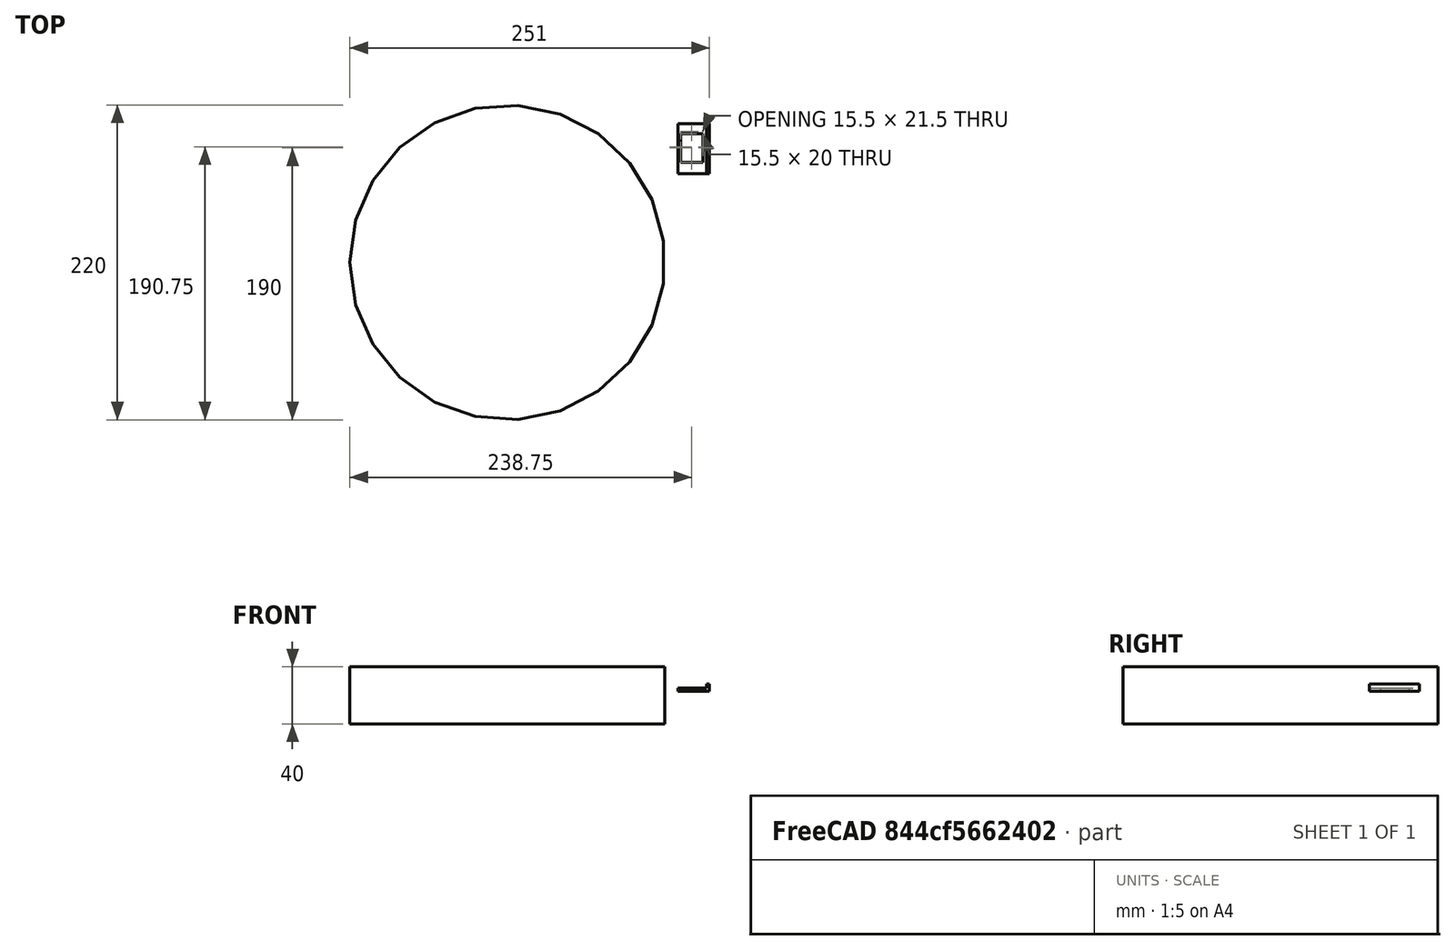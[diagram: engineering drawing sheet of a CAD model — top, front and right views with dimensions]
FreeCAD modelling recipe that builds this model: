
FCSTD DOCUMENT  (FreeCAD 0.17R13522 (Git))
Label: test_cat5
License: CreativeCommons Attribution-ShareAlike
LicenseURL: http://creativecommons.org/licenses/by-sa/4.0/
objects: Part::Box×13, Part::Cut×11, Part::Feature×3, Part::Fuse×3, Part::Extrusion×2, Part::Part2DObjectPython×1, Part::MultiFuse×1
note: 34 computed .brp shape members not serialized (recipe doc carries the construction recipe); baked Part::Feature solids carry a one-line shape summary decoded from their .brp

FEATURE [Part::Feature] Fusion002002005001001  label="apoyo superior002"
  Placement = pos=(-425,134.85,-44) rot=(1,0,0;3.14159rad)
  shape: bbox 689 x 14 x 10 mm, 7 faces (baked)
FEATURE [Part::Box] Box001  label="Cube001"
  AttacherType = Attacher::AttachEngine3D
  Height = 30
  Length = 500
  Placement = pos=(-485,0,2) rot=(0,0,1;0rad)
  Width = 30
FEATURE [Part::Cut] Cut
  Base = -> Fusion002002005001001
  Refine = true
  Tool = -> Box001
FEATURE [Part::Box] Box  label="Cube"
  AttacherType = Attacher::AttachEngine3D
  Height = 2
  Length = 288
  Width = 151.85
FEATURE [Part::Fuse] Fusion
  Base = -> Box
  Refine = true
  Tool = -> Cut
FEATURE [Part::Part2DObjectPython] Ellipse  # Draft 2D object (typed FeaturePython)
  FirstAngle = 0
  LastAngle = 0
  MajorRadius = 110
  MakeFace = true
  MinorRadius = 110
  Placement = pos=(144,-10,0) rot=(0,1,0;3.14159rad)
FEATURE [Part::Extrusion] Extrude
  Base = -> Ellipse
  Dir = (0,0,-1)
  DirMode = 2
  FaceMakerClass = Part::FaceMakerBullseye
  LengthFwd = 40
  LengthRev = 0
  Placement = pos=(0,138,22) rot=(0,0,1;0rad)
  Solid = false
  Symmetric = false
FEATURE [Part::Extrusion] Extrude001
  Base = -> Ellipse
  Dir = (0,0,-1)
  DirMode = 2
  FaceMakerClass = Part::FaceMakerBullseye
  LengthFwd = 40
  LengthRev = 0
  Placement = pos=(0,0,17) rot=(0,0,1;0rad)
  Solid = false
  Symmetric = false
FEATURE [Part::Cut] Cut001  label="la pared sin apoyos laterales"
  Base = -> Fusion
  Refine = true
  Tool = -> Extrude
FEATURE [Part::Box] Box002  label="lateral derecho"
  AttacherType = Attacher::AttachEngine3D
  Height = 3
  Length = 3
  Placement = pos=(2,17,2) rot=(0,0,1;0rad)
  Width = 127.85
FEATURE [Part::Feature] Box002001  label="lateral izquierda"
  Placement = pos=(283,17,2) rot=(0,0,1;0rad)
  shape: bbox 3 x 127.9 x 3 mm, 6 faces (baked)
FEATURE [Part::Fuse] Fusion002002005001002
  Base = -> Cut001
  Refine = true
  Tool = -> Box002
FEATURE [Part::Fuse] Fusion002002005001003
  Base = -> Box002001
  Refine = true
  Tool = -> Fusion002002005001002
FEATURE [Part::Box] Box002002  label="Cube002"
  AttacherType = Attacher::AttachEngine3D
  Height = 20
  Length = 15.5
  Placement = pos=(225,20,-4) rot=(0,0,1;0rad)
  Width = 21.5
FEATURE [Part::Box] Box002003  label="Cube003"
  AttacherType = Attacher::AttachEngine3D
  Height = 20
  Length = 15.5
  Placement = pos=(245,20,-4) rot=(0,0,1;0rad)
  Width = 21.5
FEATURE [Part::Box] Box002004  label="Cube004"
  AttacherType = Attacher::AttachEngine3D
  Height = 20
  Length = 15.5
  Placement = pos=(265,20,-4) rot=(0,0,1;0rad)
  Width = 21.5
FEATURE [Part::Box] Box002005  label="Cube005"
  AttacherType = Attacher::AttachEngine3D
  Height = 20
  Length = 15.5
  Placement = pos=(265,60,-4) rot=(0,0,1;0rad)
  Width = 21.5
FEATURE [Part::Box] Box002006  label="Cube006"
  AttacherType = Attacher::AttachEngine3D
  Height = 20
  Length = 15.5
  Placement = pos=(265,100,-4) rot=(0,0,1;0rad)
  Width = 21.5
FEATURE [Part::Cut] Cut002
  Base = -> Fusion002002005001003
  Tool = -> Box002004
FEATURE [Part::Cut] Cut003
  Base = -> Cut002
  Tool = -> Box002003
FEATURE [Part::Cut] Cut004
  Base = -> Cut003
  Tool = -> Box002002
FEATURE [Part::Cut] Cut005
  Base = -> Cut004
  Tool = -> Box002006
FEATURE [Part::Cut] Cut006  label="panel fondo con cat5"
  Base = -> Cut005
  Tool = -> Box002005
FEATURE [Part::Box] Box002007  label="Cube007"
  AttacherType = Attacher::AttachEngine3D
  Height = 40
  Length = 273
  Placement = pos=(-10,-14,-10) rot=(0,0,1;0rad)
  Width = 500
FEATURE [Part::Cut] Cut007
  Base = -> Cut006
  Tool = -> Box002007
FEATURE [Part::Box] Box002008  label="Cube008"
  AttacherType = Attacher::AttachEngine3D
  Height = 20
  Length = 60
  Placement = pos=(243,-8,-7) rot=(0,0,1;0rad)
  Width = 60
FEATURE [Part::Box] Box002009  label="Cube009"
  AttacherType = Attacher::AttachEngine3D
  Height = 20
  Length = 59
  Placement = pos=(243,87,-7) rot=(0,0,1;0rad)
  Width = 100
FEATURE [Part::Box] Box002011  label="Cube011"
  AttacherType = Attacher::AttachEngine3D
  Height = 20
  Length = 20
  Placement = pos=(285,-8,-7) rot=(0,0,1;0rad)
  Width = 100
FEATURE [Part::Cut] Cut008
  Base = -> Cut007
  Tool = -> Box002008
FEATURE [Part::Cut] Cut009
  Base = -> Cut008
  Tool = -> Box002009
FEATURE [Part::Cut] Cut010
  Base = -> Cut009
  Tool = -> Box002011
FEATURE [Part::Box] Box002012  label="Cube012"
  AttacherType = Attacher::AttachEngine3D
  Height = 2
  Length = 15.5
  Placement = pos=(265,80,0) rot=(0,0,1;0rad)
  Width = 1.5
FEATURE [Part::MultiFuse] Fusion002002005001004
  Shapes = -> [Cut010,Box002012]
FEATURE [Part::Feature] Fusion002002005001004001  label="Fusion002002005001005"
  shape: bbox 22 x 35 x 5 mm, 12 faces (baked)
